# Revit family: Sanitary_Bath-Spas_TOTO-USA-Inc_Flotation-Tub-With-ZERO-DIMENSIONR
name_source: partatom
category: Plumbing Fixtures
revit_build: Autodesk Revit 2015 (Build: 20140606_1530(x64)
units: mm (PartAtom-declared; Revit-internal decimal feet)

## types (1)
- PJYD2200PWEU
    BIMobject category = Bath & Spas
    BIMobject category code = sanitary-bath-spas
    BIMobject main category = Sanitary
    BIMobject main category code = sanitary
    Brand url = https://www.totousa.com
    Default Elevation = 4' - 0"
    Description = Flotation Tub With ZERO DIMENSION
    Edition number = 1
    Gallons = 77.5 gal to Overflow
    Installation instructions = https://www.totousa.com
    Manufacturer = TOTO
    Manufacturer name = TOTO USA Inc
    Masterformat 2014 Code = 10 28 00
    Masterformat 2014 Description = Toilet, Bath, and Laundry Accessories
    Material = Galaline - TOTO - Reinforced Marble
    Model = PJYD2200PWEU
    NBS Reference Code = 35-06-08
    NBS Reference Description = Baths
    OmniClass Code = 23-31 15 00
    OmniClass Description = Bathtubs
    Product Guid = 359806df-94ae-4627-9f39-a17fe4d806b8
    Product SKU = toto-pjyD2200pweu
    Product certification = https://www.totousa.com
    Product data url = https://bimobject.com
    Product family = Bathtubs
    Product group = ZERO DIMENSION®
    Product name = Flotation Tub With ZERO DIMENSION®
    Product url = https://www.totousa.com
    QR code = http://bimobject.com
    Rated Current = 9 A
    Rated Power Consumption = 1000 W
    Rated Voltage = 120 V
    Shipping Weight = 686.00 lb
    Technical description = https://www.totousa.com
    UNSPSC Code = 30181501
    Uniclass 1.4 Code = L7211
    Uniclass 1.4 Description = Baths
    Uniclass 2.0 Code = PR-35-06-08
    Uniclass 2.0 Description = Baths
    Uniclass 2015 Code = Pr_40_20_06_08
    Uniclass 2015 Name = Baths
    Warranty = Three Year Limited Warranty
    Youtube clip = https://youtu.be

## geometry (parser evidence)
native form markers: Sweep x3
no freeform markers — native parametric forms only
